FCSTD DOCUMENT  (FreeCAD 0.19R24267 +99 (Git))
Label: joycon_grip
License: All rights reserved
LicenseURL: http://en.wikipedia.org/wiki/All_rights_reserved
objects: Mesh::Feature×1, Part::Feature×1, PartDesign::FeatureBase×1, PartDesign::AdditiveBox×1, PartDesign::Body×1, Part::Mirroring×1
note: 6 computed .brp shape members not serialized (recipe doc carries the construction recipe); baked Part::Feature solids carry a one-line shape summary decoded from their .brp

FEATURE [Mesh::Feature] joyconleftgrip_flatV0_1  label="joyconleftgrip_flatV0.1"
FEATURE [Part::Feature] joyconleftgrip_flatV0_1001_solid  label="joyconleftgrip_flatV0_1001 (Solid)"
  shape: bbox 18.58 x 106 x 38.08 mm, 18022 faces (baked)
FEATURE [PartDesign::FeatureBase] BaseFeature
  BaseFeature = -> joyconleftgrip_flatV0_1001_solid
FEATURE [PartDesign::AdditiveBox] Box
  AttacherType = Attacher::AttachEngine3D
  AttachmentOffset = pos=(0,-45,-40) rot=(0,0,1;0rad)
  BaseFeature = -> BaseFeature
  Height = 15
  Length = 2
  MapMode = 7
  Placement = pos=(2.3,48.8427,-80.783) rot=(0,0.707107,0.707107;3.14159rad)
  Refine = true
  Support = -> [BaseFeature]
  Width = 50
FEATURE [PartDesign::Body] Body
  BaseFeature = -> joyconleftgrip_flatV0_1001_solid
  Group = -> [BaseFeature,Box]
  Origin = -> Origin
  Tip = -> Box
FEATURE [Part::Mirroring] Part__Mirroring  label="joyconleftgrip_flatV0_1001 (Solid) (Mirror #1)"
  Base = (0,0,-55)
  Normal = (0,0,1)
  Source = -> joyconleftgrip_flatV0_1001_solid
